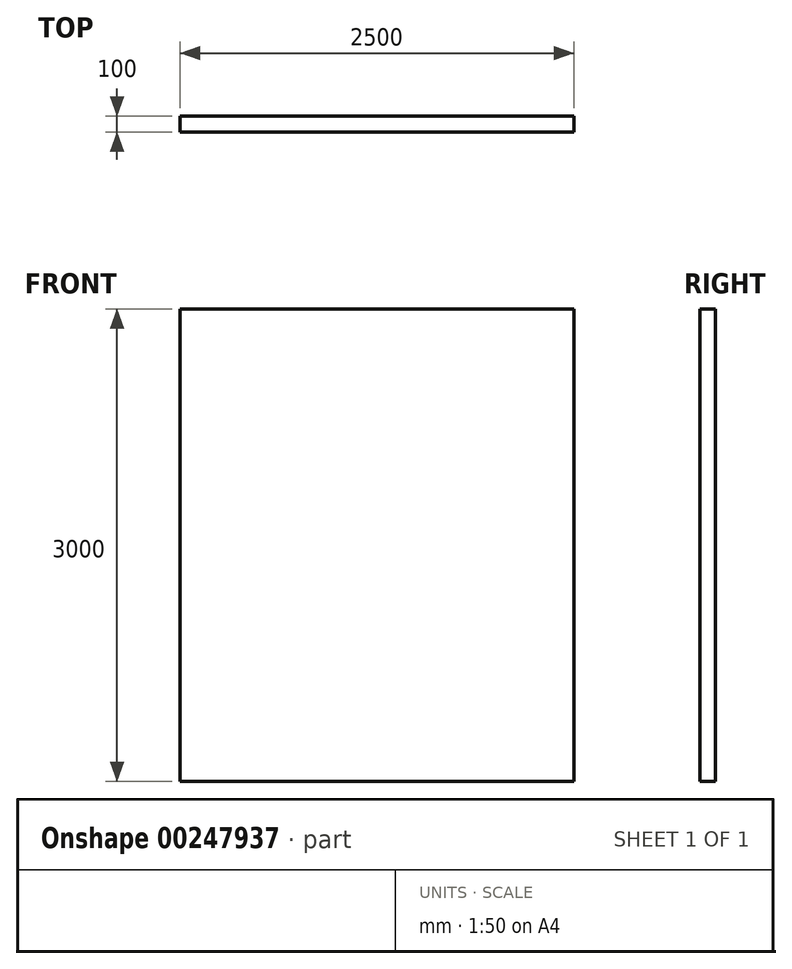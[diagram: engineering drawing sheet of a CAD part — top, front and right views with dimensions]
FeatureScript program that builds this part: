
annotation { "Feature Type Name" : "Feature", "Feature Type Description" : "" }
export const myFeature = defineFeature(function(context is Context, id is Id, definition is map)
    precondition{}
    {
        {
            var Q0;
            Q0=qCreatedBy(makeId("Front.planeOp"),FACE);
            var sketch = newSketch(context, id + "F0", { "sketchPlane" : qUnion([Q0])});
            skLineSegment(sketch, "E0.bottom", {"start": v(1250, 0) * mm, "end": v(-1250, 0) * mm});
            skLineSegment(sketch, "E0.top", {"start": v(1250, 3000) * mm, "end": v(-1250, 3000) * mm});
            skLineSegment(sketch, "E0.left", {"start": v(1250, 0) * mm, "end": v(1250, 3000) * mm});
            skLineSegment(sketch, "E0.right", {"start": v(-1250, 0) * mm, "end": v(-1250, 3000) * mm});
            skPoint(sketch, "E0.middle", {"position": v(0, 1500) * mm});
            skSolve(sketch);
        }
        {
            var Q0;
            Q0=makeQuery(id+"F0.imprint","IMPRINT",FACE,{"disambiguationData":[TD([[makeQuery(id+"F0.imprint","IMPRINT",EDGE,{"derivedFrom":sQuery(id+"F0.wireOp",EDGE,"E0.bottom")}),-1.0]])]});
            extrude(context, id + "F1", {"entities" : qUnion([Q0]), "endBound" : BoundingType.SYMMETRIC, "depth" : 100 * mm});
        }
    });
